# Revit family: Sanitary_Showers_hansgrohe_26406CHN-Vernis-Shape-Ceiling-connector_NEWWW
name_source: partatom
category: Plumbing Fixtures
revit_build: Autodesk Revit 2018 (Build: 20170223_1515(x64)
units: mm (PartAtom-declared; Revit-internal decimal feet)

## family parameters
Always vertical = No
Cut with Voids When Loaded = No
OmniClass Number = 23.31.17.00
OmniClass Title = Showers
Part Type = Normal
Room Calculation Point = No
Round Connector Dimension = Use Diameter
Shared = No
Work Plane-Based = Yes

## types (1)
- 677 Matt Black
    Always visible = Yes
    BIMobject category = Showers
    Default Elevation = 1219.2 mm  [stored 4 ft]
    Description = Vernis Shape Ceiling connector 10 cm
    Design country = Germany
    EAN code = 4059625326558
    Edition number = 1
    GTIN code = https://4059625326558
    IFC Classification = Sanitary Terminal
    Manufacturer = Hansgrohe
    Manufacturer country = Germany
    Manufacturer name = hansgrohe
    Material 1 = Hansgrohe - Metal - 677 Matt Black
    Material main = Metal
    Model = 26406CHN
    OmniClass Code = 23-31 17 00
    OmniClass Description = Showers
    Product Guid = f46721d2-a0e9-4b82-9a9b-00b57f3055c7
    Product SKU = 26406CHN
    Product data url = https://bimobject.com
    Product family = Vernis Shape
    Product group = Shower arms
    Product name = 26406CHN Vernis Shape Ceiling connector 10 cm
    QR code = https://bimobject.com
    URL = https://www.hansgrohe.com
    Water Inlet = 13 mm
    Water Inlet Description = Water Inlet 12.7mm
    Weight Net (Kg) = 0.3

note: [stored X ft] marks values corroborated as IEEE doubles in the binary element streams (Revit-internal decimal feet)

## geometry (parser evidence)
native form markers: Sweep x1
no freeform markers — native parametric forms only
